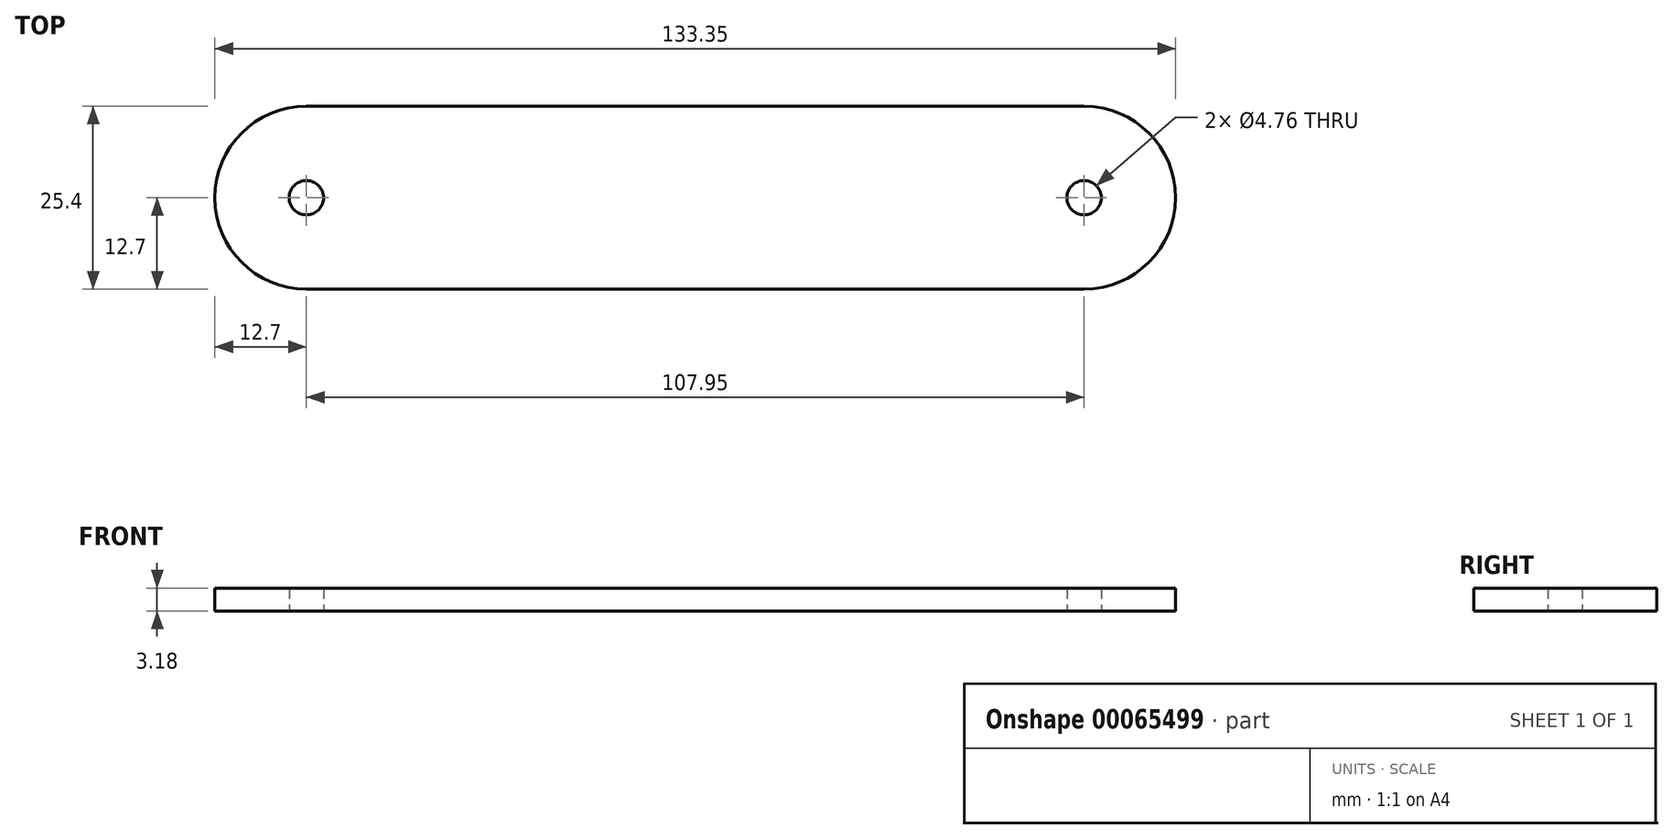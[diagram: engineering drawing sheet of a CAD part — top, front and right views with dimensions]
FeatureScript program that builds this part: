
annotation { "Feature Type Name" : "Feature", "Feature Type Description" : "" }
export const myFeature = defineFeature(function(context is Context, id is Id, definition is map)
    precondition{}
    {
        {
            var Q0;
            Q0=qCreatedBy(makeId("Top.planeOp"),FACE);
            var sketch = newSketch(context, id + "F0", { "sketchPlane" : qUnion([Q0])});
            skArc(sketch, "E0", {"start": v(0, 12.7) * mm, "mid": v(-12.7, 0) * mm, "end": v(0, -12.7) * mm});
            skLineSegment(sketch, "E1", {"start": v(0, 12.7) * mm, "end": v(107.95, 12.7) * mm});
            skLineSegment(sketch, "E2", {"start": v(0, -12.7) * mm, "end": v(107.95, -12.7) * mm});
            skArc(sketch, "E3", {"start": v(107.95, 12.7) * mm, "mid": v(120.65, 0) * mm, "end": v(107.95, -12.7) * mm});
            skCircle(sketch, "E4", {"center": v(0, 0) * mm, "radius": 2.38 * mm});
            skCircle(sketch, "E5", {"center": v(107.95, 0) * mm, "radius": 2.38 * mm});
            skSolve(sketch);
        }
        {
            var Q0;
            Q0=makeQuery(id+"F0.imprint","IMPRINT",FACE,{"disambiguationData":[TD([[makeQuery(id+"F0.imprint","IMPRINT",EDGE,{"derivedFrom":sQuery(id+"F0.wireOp",EDGE,"E0")}),1.0]])]});
            extrude(context, id + "F1", {"entities" : qUnion([Q0]), "depth" : 3.17 * mm});
        }
    });
